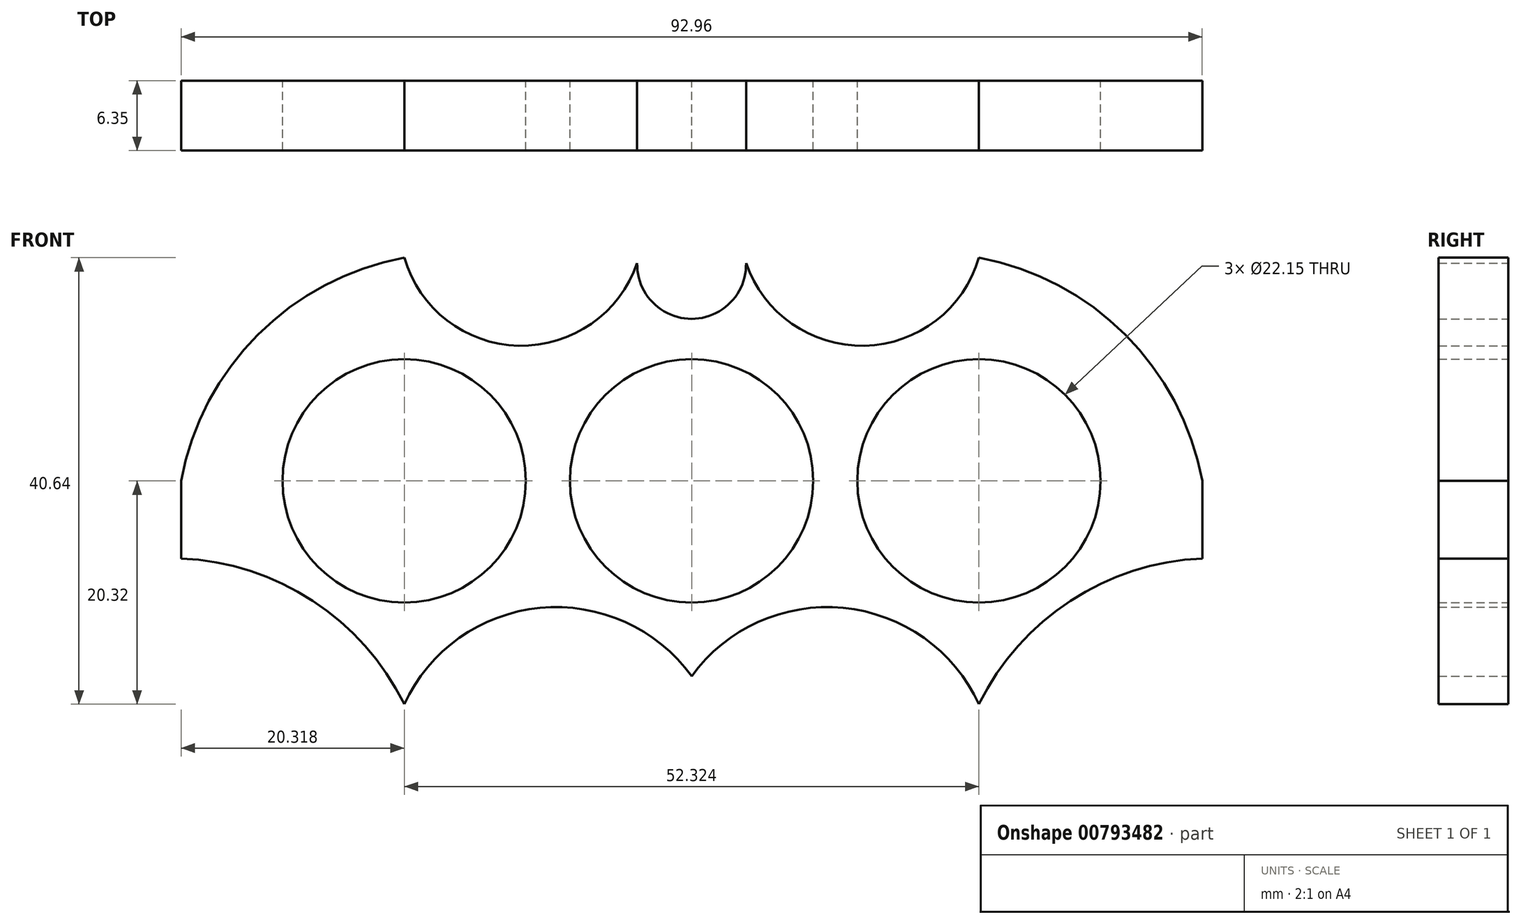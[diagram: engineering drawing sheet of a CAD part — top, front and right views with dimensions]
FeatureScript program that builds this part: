
annotation { "Feature Type Name" : "Feature", "Feature Type Description" : "" }
export const myFeature = defineFeature(function(context is Context, id is Id, definition is map)
    precondition{}
    {
        {
            var Q0;
            Q0=qCreatedBy(makeId("Front.planeOp"),FACE);
            var sketch = newSketch(context, id + "F0", { "sketchPlane" : qUnion([Q0])});
            skCircle(sketch, "E0", {"center": v(0, 0) * mm, "radius": 11.07 * mm});
            skLineSegment(sketch, "E1", {"start": v(0, 0) * mm, "end": v(26.16, 0) * mm});
            skLineSegment(sketch, "E2", {"start": v(0, 0) * mm, "end": v(-26.16, 0) * mm});
            skCircle(sketch, "E3", {"center": v(-26.16, 0) * mm, "radius": 11.07 * mm});
            skCircle(sketch, "E4", {"center": v(26.16, 0) * mm, "radius": 11.07 * mm});
            skLineSegment(sketch, "E5", {"start": v(-26.16, 0) * mm, "end": v(-26.16, 20.32) * mm});
            skLineSegment(sketch, "E6", {"start": v(26.16, 0) * mm, "end": v(26.16, 20.32) * mm});
            skLineSegment(sketch, "E7", {"start": v(-26.16, 0) * mm, "end": v(-46.48, 0) * mm});
            skLineSegment(sketch, "E8", {"start": v(26.16, 0) * mm, "end": v(46.48, 0) * mm});
            skArc(sketch, "E9", {"start": v(-26.16, 20.32) * mm, "mid": v(-39.47, 13.3) * mm, "end": v(-46.48, 0) * mm});
            skArc(sketch, "E10", {"start": v(46.48, 0) * mm, "mid": v(39.47, 13.3) * mm, "end": v(26.16, 20.32) * mm});
            skLineSegment(sketch, "E11", {"start": v(-26.16, 0) * mm, "end": v(-26.16, -20.32) * mm});
            skLineSegment(sketch, "E12", {"start": v(26.16, 0) * mm, "end": v(26.16, -20.32) * mm});
            skLineSegment(sketch, "E13", {"start": v(0, 0) * mm, "end": v(0, -17.78) * mm});
            skArc(sketch, "E14", {"start": v(0, -17.78) * mm, "mid": v(-13.8, -11.56) * mm, "end": v(-26.16, -20.32) * mm});
            skArc(sketch, "E15", {"start": v(26.16, -20.32) * mm, "mid": v(13.8, -11.56) * mm, "end": v(0, -17.78) * mm});
            skLineSegment(sketch, "E16", {"start": v(0, 2.05) * mm, "end": v(0, 14.75) * mm});
            skLineSegment(sketch, "E17", {"start": v(0, 14.75) * mm, "end": v(-4.95, 14.75) * mm});
            skLineSegment(sketch, "E18", {"start": v(0, 14.75) * mm, "end": v(4.95, 14.75) * mm});
            skLineSegment(sketch, "E19", {"start": v(-4.95, 14.75) * mm, "end": v(-4.95, 19.83) * mm});
            skLineSegment(sketch, "E20", {"start": v(4.95, 14.75) * mm, "end": v(4.95, 19.83) * mm});
            skArc(sketch, "E21", {"start": v(-4.95, 19.83) * mm, "mid": v(0, 14.75) * mm, "end": v(4.95, 19.83) * mm});
            skArc(sketch, "E22", {"start": v(-26.16, 20.32) * mm, "mid": v(-15.74, 12.3) * mm, "end": v(-4.95, 19.83) * mm});
            skArc(sketch, "E23", {"start": v(4.95, 19.83) * mm, "mid": v(15.74, 12.3) * mm, "end": v(26.16, 20.32) * mm});
            skLineSegment(sketch, "E24", {"start": v(46.48, 0) * mm, "end": v(46.48, -7.06) * mm});
            skLineSegment(sketch, "E25", {"start": v(-46.48, 0) * mm, "end": v(-46.48, -7.06) * mm});
            skArc(sketch, "E26", {"start": v(-26.16, -20.32) * mm, "mid": v(-34.5, -10.9) * mm, "end": v(-46.48, -7.06) * mm});
            skArc(sketch, "E27", {"start": v(46.48, -7.06) * mm, "mid": v(34.5, -10.9) * mm, "end": v(26.16, -20.32) * mm});
            skSolve(sketch);
        }
        {
            var Q0;
            {var subQ5=sQuery(id+"F0.wireOp",EDGE,"E9");Q0=makeQuery(id+"F0.imprint","IMPRINT",FACE,{"disambiguationData":[TD([[makeQuery(id+"F0.imprint","IMPRINT",EDGE,{"derivedFrom":subQ5}),1.0]])]});}
            var Q1;
            {var subQ0=sQuery(id+"F0.wireOp",EDGE,"E25");Q1=makeQuery(id+"F0.imprint","IMPRINT",FACE,{"disambiguationData":[TD([[makeQuery(id+"F0.imprint","IMPRINT",EDGE,{"derivedFrom":subQ0}),1.0]])]});}
            var Q2;
            {var subQ0=sQuery(id+"F0.wireOp",EDGE,"E14");Q2=makeQuery(id+"F0.imprint","IMPRINT",FACE,{"disambiguationData":[TD([[makeQuery(id+"F0.imprint","IMPRINT",EDGE,{"derivedFrom":subQ0}),-1.0]])]});}
            var Q3;
            {var subQ0=sQuery(id+"F0.wireOp",EDGE,"E15");Q3=makeQuery(id+"F0.imprint","IMPRINT",FACE,{"disambiguationData":[TD([[makeQuery(id+"F0.imprint","IMPRINT",EDGE,{"derivedFrom":subQ0}),-1.0]])]});}
            var Q4;
            {var subQ0=sQuery(id+"F0.wireOp",EDGE,"E24");Q4=makeQuery(id+"F0.imprint","IMPRINT",FACE,{"disambiguationData":[TD([[makeQuery(id+"F0.imprint","IMPRINT",EDGE,{"derivedFrom":subQ0}),-1.0]])]});}
            var Q5;
            {var subQ5=sQuery(id+"F0.wireOp",EDGE,"E10");Q5=makeQuery(id+"F0.imprint","IMPRINT",FACE,{"disambiguationData":[TD([[makeQuery(id+"F0.imprint","IMPRINT",EDGE,{"derivedFrom":subQ5}),1.0]])]});}
            var Q6;
            {var subQ8=sQuery(id+"F0.wireOp",EDGE,"E18");Q6=makeQuery(id+"F0.imprint","IMPRINT",FACE,{"disambiguationData":[TD([[makeQuery(id+"F0.imprint","IMPRINT",EDGE,{"derivedFrom":subQ8}),-1.0]])]});}
            var Q7;
            {var subQ13=sQuery(id+"F0.wireOp",EDGE,"E17");Q7=makeQuery(id+"F0.imprint","IMPRINT",FACE,{"disambiguationData":[TD([[makeQuery(id+"F0.imprint","IMPRINT",EDGE,{"derivedFrom":subQ13}),1.0]])]});}
            var Q8;
            {var subQ0=sQuery(id+"F0.wireOp",EDGE,"E17");Q8=makeQuery(id+"F0.imprint","IMPRINT",FACE,{"disambiguationData":[TD([[makeQuery(id+"F0.imprint","IMPRINT",EDGE,{"derivedFrom":subQ0}),-1.0]])]});}
            var Q9;
            {var subQ0=sQuery(id+"F0.wireOp",EDGE,"E18");Q9=makeQuery(id+"F0.imprint","IMPRINT",FACE,{"disambiguationData":[TD([[makeQuery(id+"F0.imprint","IMPRINT",EDGE,{"derivedFrom":subQ0}),1.0]])]});}
            extrude(context, id + "F1", {"entities" : qUnion([Q0, Q1, Q2, Q3, Q4, Q5, Q6, Q7, Q8, Q9]), "depth" : 6.35 * mm, "offsetDistance" : 25.4 * mm});
        }
    });
